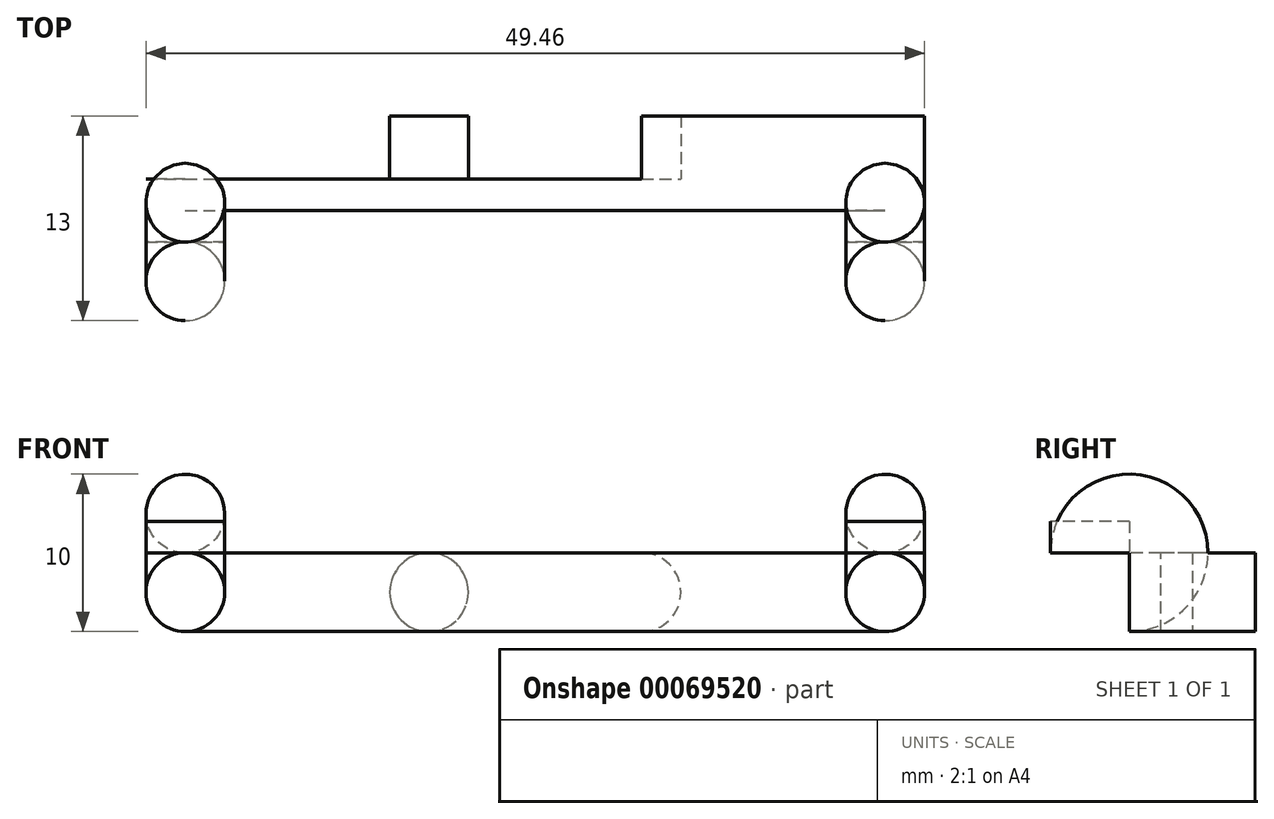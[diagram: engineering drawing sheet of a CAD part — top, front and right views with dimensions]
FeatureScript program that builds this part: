
annotation { "Feature Type Name" : "Feature", "Feature Type Description" : "" }
export const myFeature = defineFeature(function(context is Context, id is Id, definition is map)
    precondition{}
    {
        {
            var Q0;
            Q0=qCreatedBy(makeId("Front.planeOp"),FACE);
            var sketch = newSketch(context, id + "F0", { "sketchPlane" : qUnion([Q0])});
            skLineSegment(sketch, "E0", {"start": v(0, 0) * mm, "end": v(0, 50) * mm, "construction": true});
            skLineSegment(sketch, "E1", {"start": v(0, 0) * mm, "end": v(-22.23, 0) * mm, "construction": true});
            skLineSegment(sketch, "E2.MirrorCS", {"start": v(0, 0) * mm, "end": v(22.23, 0) * mm, "construction": true});
            skCircle(sketch, "E3", {"center": v(-22.23, 0) * mm, "radius": 2.5 * mm});
            skLineSegment(sketch, "E4.bottom", {"start": v(-22.23, -2.5) * mm, "end": v(22.23, -2.5) * mm});
            skLineSegment(sketch, "E4.top", {"start": v(-22.23, 2.5) * mm, "end": v(22.23, 2.5) * mm});
            skLineSegment(sketch, "E4.left", {"start": v(-22.23, -2.5) * mm, "end": v(-22.23, 2.5) * mm});
            skLineSegment(sketch, "E4.right", {"start": v(22.23, -2.5) * mm, "end": v(22.23, 2.5) * mm});
            skPoint(sketch, "E4.middle", {"position": v(0, 0) * mm});
            skCircle(sketch, "E5.MirrorC", {"center": v(22.23, 0) * mm, "radius": 2.5 * mm});
            skSolve(sketch);
        }
        {
            var Q0;
            Q0 = qSketchRegion(id + "F0", true);
            var Q1;
            Q1=makeQuery(id+"F0.imprint","IMPRINT",FACE,{"disambiguationData":[TD([[makeQuery(id+"F0.imprint","IMPRINT",EDGE,{"derivedFrom":sQuery(id+"F0.wireOp",EDGE,"E3")}),1.0]])]});
            var Q2;
            Q2=makeQuery(id+"F0.imprint","IMPRINT",FACE,{"disambiguationData":[TD([[makeQuery(id+"F0.imprint","IMPRINT",EDGE,{"derivedFrom":sQuery(id+"F0.wireOp",EDGE,"E5.MirrorC")}),-1.0]])]});
            extrude(context, id + "F1", {"entities" : qUnion([Q0, Q1, Q2]), "oppositeDirection" : true, "depth" : 2 * mm});
        }
        {
            var Q0;
            {var subQ0=sQuery(id+"F0.wireOp",EDGE,"E4.left");Q0=makeQuery(id+"F0.imprint","IMPRINT",FACE,{"disambiguationData":[TD([[makeQuery(id+"F0.imprint","IMPRINT",EDGE,{"derivedFrom":subQ0}),1.0]])]});}
            var Q1;
            {var subQ0=sQuery(id+"F0.wireOp",EDGE,"E4.left");Q1=makeQuery(id+"F0.imprint","IMPRINT",FACE,{"disambiguationData":[TD([[makeQuery(id+"F0.imprint","IMPRINT",EDGE,{"derivedFrom":subQ0}),-1.0]])]});}
            var Q2;
            {var subQ0=sQuery(id+"F0.wireOp",EDGE,"E4.right");Q2=makeQuery(id+"F0.imprint","IMPRINT",FACE,{"disambiguationData":[TD([[makeQuery(id+"F0.imprint","IMPRINT",EDGE,{"derivedFrom":subQ0}),-1.0]])]});}
            var Q3;
            {var subQ0=sQuery(id+"F0.wireOp",EDGE,"E4.right");Q3=makeQuery(id+"F0.imprint","IMPRINT",FACE,{"disambiguationData":[TD([[makeQuery(id+"F0.imprint","IMPRINT",EDGE,{"derivedFrom":subQ0}),1.0]])]});}
            var Q4;
            Q4=sQuery(id+"F0.wireOp",EDGE,"E5.MirrorC");
            var Q5;
            Q5=sQuery(id+"F0.wireOp",EDGE,"E4.left");
            var Q6;
            Q6=sQuery(id+"F0.wireOp",EDGE,"E3");
            extrude(context, id + "F2", {"entities" : qUnion([Q0, Q1, Q2, Q3]), "operationType" : NewBodyOperationType.ADD, "surfaceEntities" : qUnion([Q4, Q5, Q6]), "depth" : 2 * mm});
        }
        {
            var Q0;
            Q0=makeQuery(id+"F2.opExtrude","CAP_FACE",FACE,{"disambiguationData":[OSD([sQuery(id+"F0.wireOp",EDGE,"E3")])],"isStart":false});
            var sketch = newSketch(context, id + "F3", { "sketchPlane" : qUnion([Q0])});
            skLineSegment(sketch, "E6", {"start": v(-22.23, 2.5) * mm, "end": v(22.66, 2.5) * mm, "construction": true});
            skSolve(sketch);
        }
        {
            var Q0;
            Q0=makeQuery(id+"F3.imprint","IMPRINT",FACE,{"disambiguationData":[TD([[makeQuery(id+"F3.imprint","IMPRINT",EDGE,{"derivedFrom":makeQuery(id+"F2.opExtrude","CAP_EDGE",EDGE,{"disambiguationData":[OSD([sQuery(id+"F0.wireOp",EDGE,"E3")])],"isStart":false})}),1.0]])]});
            var Q1;
            Q1=makeQuery(id+"F2.opExtrude","CAP_FACE",FACE,{"disambiguationData":[OSD([sQuery(id+"F0.wireOp",EDGE,"E5.MirrorC")])],"isStart":false});
            var Q2;
            Q2=sQuery(id+"F3.wireOp",EDGE,"E6");
            revolve(context, id + "F4", {"operationType" : NewBodyOperationType.ADD, "entities" : qUnion([Q0, Q1]), "axis" : qUnion([Q2]), "revolveType" : RevolveType.ONE_DIRECTION, "oppositeDirection" : true, "angle" : 90 * degree});
        }
        {
            var Q0;
            Q0=makeQuery(id+"F4.opRevolve","CAP_FACE",FACE,{"disambiguationData":[OSD([sQuery(id+"F0.wireOp",EDGE,"E3")])],"isStart":false});
            var Q1;
            Q1=makeQuery(id+"F4.opRevolve","CAP_FACE",FACE,{"disambiguationData":[OSD([sQuery(id+"F0.wireOp",EDGE,"E5.MirrorC")])],"isStart":false});
            extrude(context, id + "F5", {"entities" : qUnion([Q0, Q1]), "operationType" : NewBodyOperationType.ADD, "depth" : 2 * mm});
        }
        {
            var Q0;
            Q0=makeQuery(id+"F1.opExtrude","CAP_FACE",FACE,{"disambiguationData":[OSD([sQuery(id+"F0.wireOp",EDGE,"E3"),sQuery(id+"F0.wireOp",EDGE,"E4.bottom"),sQuery(id+"F0.wireOp",EDGE,"E4.top"),sQuery(id+"F0.wireOp",EDGE,"E5.MirrorC")])],"isStart":false});
            var sketch = newSketch(context, id + "F6", { "sketchPlane" : qUnion([Q0])});
            skLineSegment(sketch, "E7", {"start": v(24.73, 0) * mm, "end": v(-24.73, 0) * mm, "construction": true});
            skPoint(sketch, "E8", {"position": v(6.75, 0) * mm});
            skPoint(sketch, "E9.MirrorP", {"position": v(-6.75, 0) * mm});
            skCircle(sketch, "E10", {"center": v(6.75, 0) * mm, "radius": 2.5 * mm});
            skCircle(sketch, "E11.MirrorC", {"center": v(-6.75, 0) * mm, "radius": 2.5 * mm});
            skSolve(sketch);
        }
        {
            var Q0;
            {var subQ0=sQuery(id+"F6.wireOp",EDGE,"E10");var subQ1=makeQuery(id+"F6.imprint","INTERSECT",VERTEX,{"derivedFrom":[makeQuery(id+"F1.opExtrude","CAP_EDGE",EDGE,{"disambiguationData":[OSD([sQuery(id+"F0.wireOp",EDGE,"E4.bottom")])],"isStart":false}),subQ0]});Q0=makeQuery(id+"F6.imprint","IMPRINT",FACE,{"disambiguationData":[TD([[makeQuery(id+"F6.imprint","IMPRINT",EDGE,{"disambiguationData":[TD([[subQ1,1.0]])],"derivedFrom":subQ0}),1.0]])]});}
            var Q1;
            {var subQ0=sQuery(id+"F6.wireOp",EDGE,"E11.MirrorC");var subQ1=makeQuery(id+"F6.imprint","INTERSECT",VERTEX,{"derivedFrom":[makeQuery(id+"F1.opExtrude","CAP_EDGE",EDGE,{"disambiguationData":[OSD([sQuery(id+"F0.wireOp",EDGE,"E4.bottom")])],"isStart":false}),subQ0]});Q1=makeQuery(id+"F6.imprint","IMPRINT",FACE,{"disambiguationData":[TD([[makeQuery(id+"F6.imprint","IMPRINT",EDGE,{"disambiguationData":[TD([[subQ1,1.0]])],"derivedFrom":subQ0}),-1.0]])]});}
            extrude(context, id + "F7", {"entities" : qUnion([Q0, Q1]), "operationType" : NewBodyOperationType.ADD, "depth" : 4 * mm});
        }
    });
